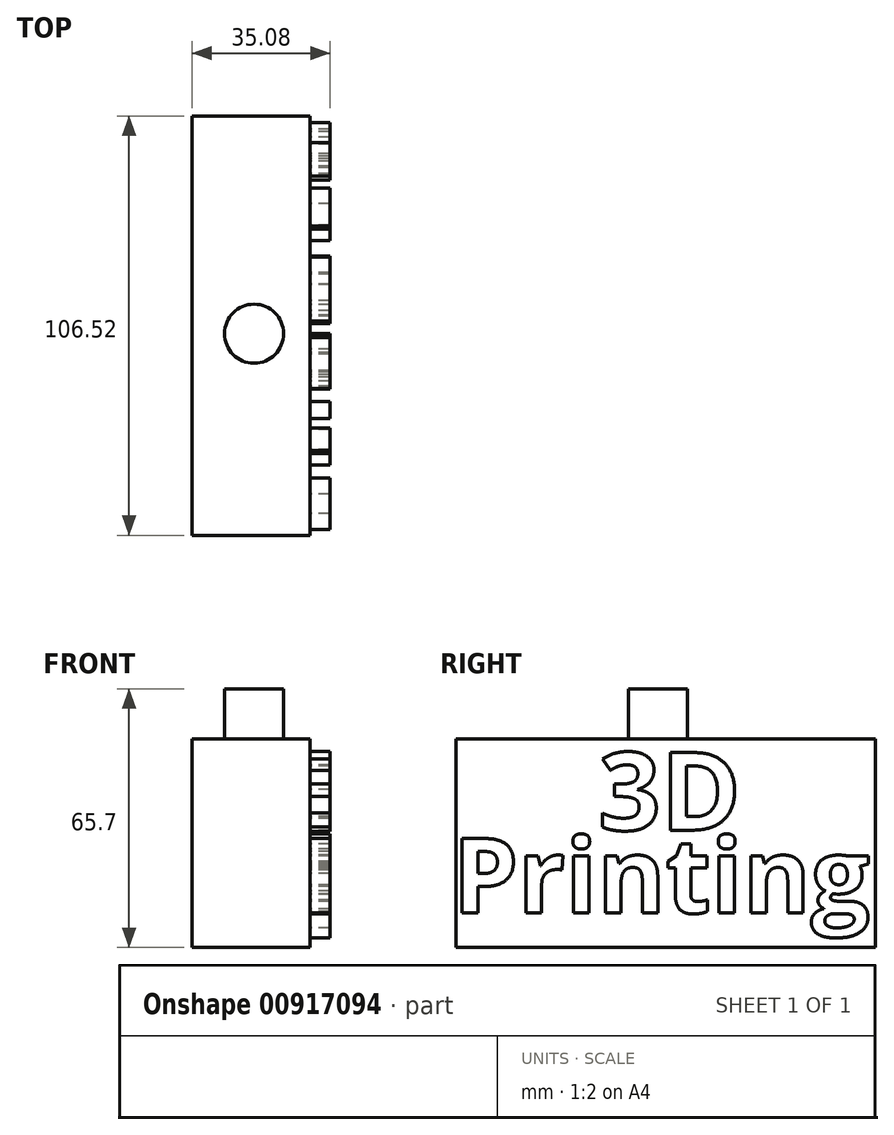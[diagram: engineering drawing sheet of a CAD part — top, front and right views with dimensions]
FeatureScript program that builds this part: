
annotation { "Feature Type Name" : "Feature", "Feature Type Description" : "" }
export const myFeature = defineFeature(function(context is Context, id is Id, definition is map)
    precondition{}
    {
        {
            var Q0;
            Q0=qCreatedBy(makeId("Right.planeOp"),FACE);
            var sketch = newSketch(context, id + "F0", { "sketchPlane" : qUnion([Q0])});
            skLineSegment(sketch, "E0.bottom", {"start": v(-51.23, -12.06) * mm, "end": v(55.3, -12.06) * mm});
            skLineSegment(sketch, "E0.top", {"start": v(-51.23, -65.06) * mm, "end": v(55.3, -65.06) * mm});
            skLineSegment(sketch, "E0.left", {"start": v(-51.23, -12.06) * mm, "end": v(-51.23, -65.06) * mm});
            skLineSegment(sketch, "E0.right", {"start": v(55.3, -12.06) * mm, "end": v(55.3, -65.06) * mm});
            skSolve(sketch);
        }
        {
            var Q0;
            Q0 = qSketchRegion(id + "F0", true);
            extrude(context, id + "F1", {"entities" : qUnion([Q0]), "depth" : 30 * mm, "offsetDistance" : 25.4 * mm});
        }
        {
            var Q0;
            Q0=makeQuery(id+"F1.opExtrude","CAP_FACE",FACE,{"disambiguationData":[OSD([sQuery(id+"F0.wireOp",EDGE,"E0.bottom"),sQuery(id+"F0.wireOp",EDGE,"E0.top"),sQuery(id+"F0.wireOp",EDGE,"E0.left"),sQuery(id+"F0.wireOp",EDGE,"E0.right")])],"isStart":false});
            var sketch = newSketch(context, id + "F2", { "sketchPlane" : qUnion([Q0])});
            skText(sketch, "E1", { "text": "3D", "fontName": "OpenSans-Bold.ttf"});
            skText(sketch, "E2", { "text": "Printing", "fontName": "OpenSans-Bold.ttf"});
            const initialGuessF2  = {"E1": [-0.01506, -0.03527, 1, 0, 0.01987], "E2": [-0.0521, -0.0563, 1, 0, 0.01905]};
            skSetInitialGuess(sketch, initialGuessF2);
            skSolve(sketch);
        }
        {
            var Q0;
            Q0 = qSketchRegion(id + "F2", true);
            extrude(context, id + "F3", {"entities" : qUnion([Q0]), "operationType" : NewBodyOperationType.ADD, "depth" : 5.08 * mm, "offsetDistance" : 25.4 * mm});
        }
        {
            var Q0;
            Q0=makeQuery(id+"F1.opExtrude","SWEPT_FACE",FACE,{"disambiguationData":[OSD([sQuery(id+"F0.wireOp",EDGE,"E0.bottom")])]});
            var sketch = newSketch(context, id + "F4", { "sketchPlane" : qUnion([Q0])});
            skCircle(sketch, "E3", {"center": v(15.75, 0) * mm, "radius": 7.5 * mm});
            skSolve(sketch);
        }
        {
            var Q0;
            Q0=makeQuery(id+"F4.imprint","IMPRINT",FACE,{"disambiguationData":[TD([[makeQuery(id+"F4.imprint","IMPRINT",EDGE,{"derivedFrom":sQuery(id+"F4.wireOp",EDGE,"E3")}),1.0]])]});
            var Q1;
            Q1=sQuery(id+"F4.wireOp",EDGE,"E3");
            extrude(context, id + "F5", {"entities" : qUnion([Q0]), "operationType" : NewBodyOperationType.ADD, "surfaceOperationType" : NewSurfaceOperationType.ADD, "surfaceEntities" : qUnion([Q1]), "depth" : 12.7 * mm, "offsetDistance" : 25.4 * mm});
        }
    });
